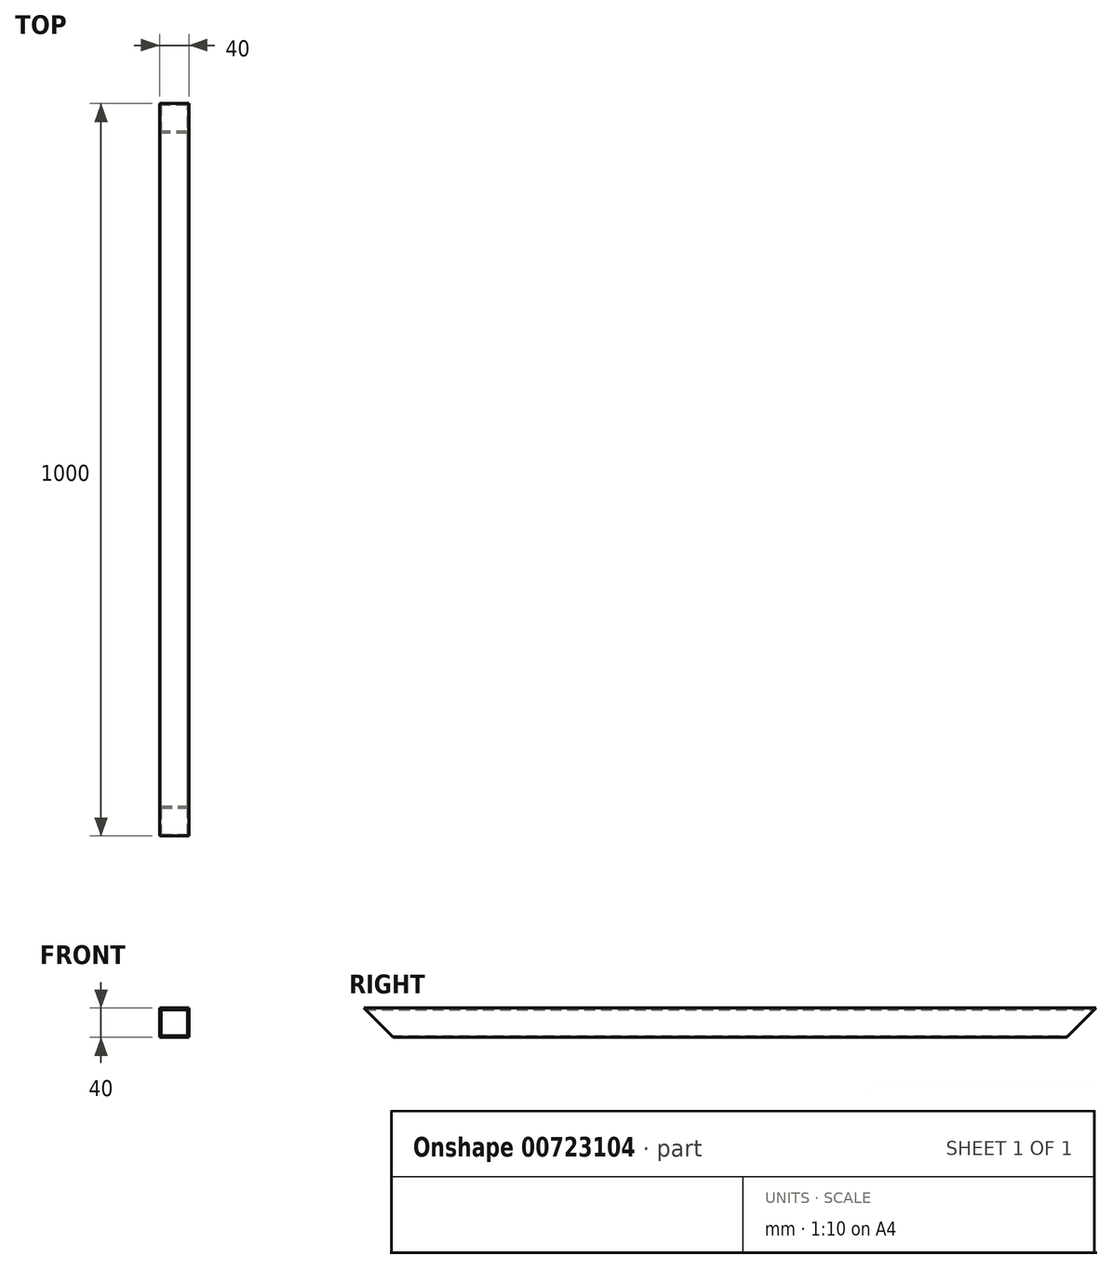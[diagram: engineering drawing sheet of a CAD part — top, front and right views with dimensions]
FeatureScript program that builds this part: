
annotation { "Feature Type Name" : "Feature", "Feature Type Description" : "" }
export const myFeature = defineFeature(function(context is Context, id is Id, definition is map)
    precondition{}
    {
        {
            var Q0;
            Q0=qCreatedBy(makeId("Front.planeOp"),FACE);
            var sketch = newSketch(context, id + "F0", { "sketchPlane" : qUnion([Q0])});
            skLineSegment(sketch, "E0.bottom", {"start": v(0, 0) * mm, "end": v(40, 0) * mm});
            skLineSegment(sketch, "E0.top", {"start": v(0, 40) * mm, "end": v(40, 40) * mm});
            skLineSegment(sketch, "E0.left", {"start": v(0, 0) * mm, "end": v(0, 40) * mm});
            skLineSegment(sketch, "E0.right", {"start": v(40, 0) * mm, "end": v(40, 40) * mm});
            skLineSegment(sketch, "E1.bottom", {"start": v(2, 2) * mm, "end": v(38, 2) * mm});
            skLineSegment(sketch, "E1.top", {"start": v(2, 38) * mm, "end": v(38, 38) * mm});
            skLineSegment(sketch, "E1.left", {"start": v(2, 2) * mm, "end": v(2, 38) * mm});
            skLineSegment(sketch, "E1.right", {"start": v(38, 2) * mm, "end": v(38, 38) * mm});
            skSolve(sketch);
        }
        {
            var Q0;
            Q0 = qSketchRegion(id + "F0", true);
            extrude(context, id + "F1", {"entities" : qUnion([Q0]), "depth" : 1000 * mm, "offsetDistance" : 25 * mm});
        }
        {
            var Q0;
            Q0=makeQuery(id+"F1.opExtrude","CAP_EDGE",EDGE,{"disambiguationData":[OSD([sQuery(id+"F0.wireOp",EDGE,"E0.bottom")])],"isStart":false});
            var Q1;
            Q1=makeQuery(id+"F1.opExtrude","CAP_EDGE",EDGE,{"disambiguationData":[OSD([sQuery(id+"F0.wireOp",EDGE,"E0.bottom")])],"isStart":true});
            chamfer(context, id + "F2", {"entities" : qUnion([Q0, Q1]), "width" : 40 * mm, "tangentPropagation" : true});
        }
    });
